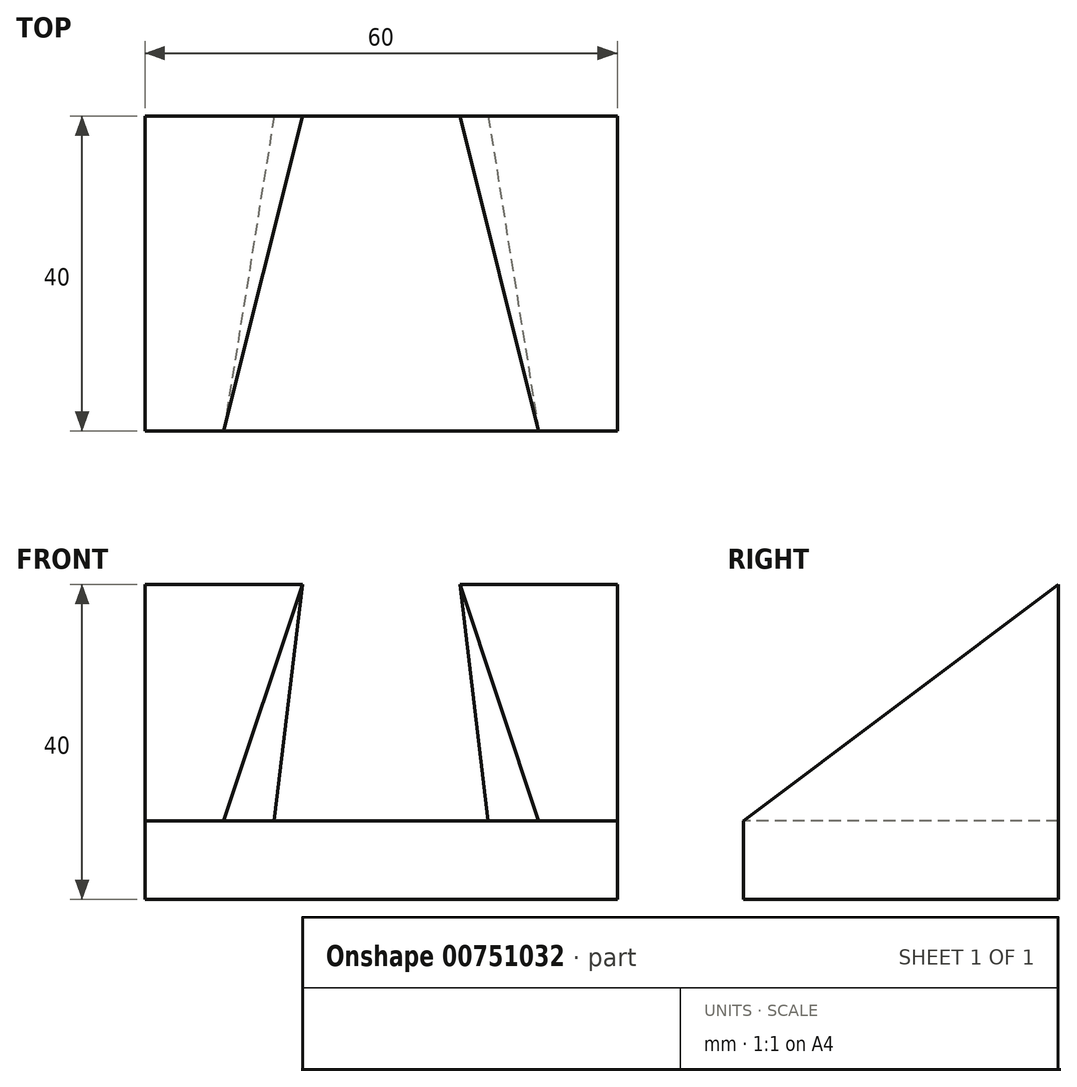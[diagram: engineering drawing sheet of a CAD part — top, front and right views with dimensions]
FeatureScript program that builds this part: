
annotation { "Feature Type Name" : "Feature", "Feature Type Description" : "" }
export const myFeature = defineFeature(function(context is Context, id is Id, definition is map)
    precondition{}
    {
        {
            var Q0;
            Q0=qCreatedBy(makeId("Front.planeOp"),FACE);
            var sketch = newSketch(context, id + "F0", { "sketchPlane" : qUnion([Q0])});
            skLineSegment(sketch, "E0", {"start": v(0, 0) * mm, "end": v(60, 0) * mm});
            skLineSegment(sketch, "E1", {"start": v(60, 0) * mm, "end": v(60, 40) * mm});
            skLineSegment(sketch, "E2", {"start": v(60, 40) * mm, "end": v(40, 40) * mm});
            skLineSegment(sketch, "E3", {"start": v(40, 40) * mm, "end": v(40, 10) * mm});
            skLineSegment(sketch, "E4", {"start": v(40, 10) * mm, "end": v(20, 10) * mm});
            skLineSegment(sketch, "E5", {"start": v(20, 10) * mm, "end": v(20, 40) * mm});
            skLineSegment(sketch, "E6", {"start": v(20, 40) * mm, "end": v(0, 40) * mm});
            skLineSegment(sketch, "E7", {"start": v(0, 40) * mm, "end": v(0, 0) * mm});
            skSolve(sketch);
        }
        {
            var Q0;
            Q0=makeQuery(id+"F0.imprint","IMPRINT",FACE,{"disambiguationData":[TD([[makeQuery(id+"F0.imprint","IMPRINT",EDGE,{"derivedFrom":sQuery(id+"F0.wireOp",EDGE,"E0")}),1.0]])]});
            extrude(context, id + "F1", {"entities" : qUnion([Q0]), "depth" : 40 * mm, "offsetDistance" : 25 * mm});
        }
        {
            var Q0;
            Q0=makeQuery(id+"F1.opExtrude","SWEPT_FACE",FACE,{"disambiguationData":[OSD([sQuery(id+"F0.wireOp",EDGE,"E1")])]});
            var sketch = newSketch(context, id + "F2", { "sketchPlane" : qUnion([Q0])});
            skLineSegment(sketch, "E8", {"start": v(0, 40) * mm, "end": v(0, 10) * mm});
            skLineSegment(sketch, "E9", {"start": v(0, 10) * mm, "end": v(-40, 10) * mm});
            skLineSegment(sketch, "E10", {"start": v(-40, 10) * mm, "end": v(0, 40) * mm});
            skSolve(sketch);
        }
        {
            var Q0;
            {var subQ0=sQuery(id+"F2.wireOp",EDGE,"E10");Q0=makeQuery(id+"F2.imprint","IMPRINT",FACE,{"disambiguationData":[TD([[makeQuery(id+"F2.imprint","IMPRINT",EDGE,{"derivedFrom":subQ0}),1.0]])]});}
            extrude(context, id + "F3", {"entities" : qUnion([Q0]), "operationType" : NewBodyOperationType.REMOVE, "oppositeDirection" : true, "depth" : 60 * mm, "offsetDistance" : 25 * mm});
        }
        {
            var Q0;
            {var subQ0=sQuery(id+"F0.wireOp",EDGE,"E5");Q0=makeQuery(id+"F3.boolean.opBoolean","COPY",FACE,{"disambiguationData":[TD([makeQuery(id+"F1.opExtrude","SWEPT_FACE",FACE,{"disambiguationData":[OSD([subQ0])]})])],"derivedFrom":makeQuery(id+"F3.opExtrude","SWEPT_FACE",FACE,{"disambiguationData":[OSD([sQuery(id+"F2.wireOp",EDGE,"E10")])]})});}
            var sketch = newSketch(context, id + "F4", { "sketchPlane" : qUnion([Q0])});
            skLineSegment(sketch, "E11", {"start": v(20, 24) * mm, "end": v(10, -26) * mm});
            skLineSegment(sketch, "E12", {"start": v(10, -26) * mm, "end": v(20, -26) * mm});
            skLineSegment(sketch, "E13", {"start": v(20, -26) * mm, "end": v(20, 24) * mm});
            skSolve(sketch);
        }
        {
            var Q0;
            Q0=makeQuery(id+"F4.imprint","IMPRINT",FACE,{"disambiguationData":[TD([[makeQuery(id+"F4.imprint","IMPRINT",EDGE,{"derivedFrom":sQuery(id+"F4.wireOp",EDGE,"E11")}),1.0]])]});
            extrude(context, id + "F5", {"entities" : qUnion([Q0]), "operationType" : NewBodyOperationType.REMOVE, "oppositeDirection" : true, "depth" : 40 * mm, "offsetDistance" : 25 * mm});
        }
        {
            var Q0;
            {var subQ1=sQuery(id+"F0.wireOp",EDGE,"E1");Q0=makeQuery(id+"F3.boolean.opBoolean","COPY",FACE,{"disambiguationData":[TD([makeQuery(id+"F1.opExtrude","SWEPT_FACE",FACE,{"disambiguationData":[OSD([subQ1])]})])],"derivedFrom":makeQuery(id+"F3.opExtrude","SWEPT_FACE",FACE,{"disambiguationData":[OSD([sQuery(id+"F2.wireOp",EDGE,"E10")])]})});}
            var sketch = newSketch(context, id + "F6", { "sketchPlane" : qUnion([Q0])});
            skLineSegment(sketch, "E14", {"start": v(40, 24) * mm, "end": v(50, -26) * mm});
            skLineSegment(sketch, "E15", {"start": v(50, -26) * mm, "end": v(40, -26) * mm});
            skLineSegment(sketch, "E16", {"start": v(40, -26) * mm, "end": v(40, 24) * mm});
            skSolve(sketch);
        }
        {
            var Q0;
            Q0=makeQuery(id+"F6.imprint","IMPRINT",FACE,{"disambiguationData":[TD([[makeQuery(id+"F6.imprint","IMPRINT",EDGE,{"derivedFrom":sQuery(id+"F6.wireOp",EDGE,"E14")}),-1.0]])]});
            extrude(context, id + "F7", {"entities" : qUnion([Q0]), "operationType" : NewBodyOperationType.REMOVE, "oppositeDirection" : true, "depth" : 40 * mm, "offsetDistance" : 25 * mm});
        }
        {
            var Q0;
            Q0=makeQuery(id+"F1.opExtrude","CAP_FACE",FACE,{"disambiguationData":[OSD([sQuery(id+"F0.wireOp",EDGE,"E0"),sQuery(id+"F0.wireOp",EDGE,"E1"),sQuery(id+"F0.wireOp",EDGE,"E2"),sQuery(id+"F0.wireOp",EDGE,"E3"),sQuery(id+"F0.wireOp",EDGE,"E4"),sQuery(id+"F0.wireOp",EDGE,"E5"),sQuery(id+"F0.wireOp",EDGE,"E6"),sQuery(id+"F0.wireOp",EDGE,"E7")])],"isStart":false});
            var sketch = newSketch(context, id + "F8", { "sketchPlane" : qUnion([Q0])});
            skLineSegment(sketch, "E17", {"start": v(10, 10) * mm, "end": v(20, 10) * mm});
            skLineSegment(sketch, "E18", {"start": v(20, 10) * mm, "end": v(20, 0) * mm});
            skLineSegment(sketch, "E19", {"start": v(20, 0) * mm, "end": v(10, 0) * mm});
            skLineSegment(sketch, "E20", {"start": v(10, 0) * mm, "end": v(10, 10) * mm});
            skSolve(sketch);
        }
        {
            var Q0;
            Q0=makeQuery(id+"F8.imprint","IMPRINT",FACE,{"disambiguationData":[TD([[makeQuery(id+"F8.imprint","IMPRINT",EDGE,{"derivedFrom":sQuery(id+"F8.wireOp",EDGE,"E17")}),-1.0]])]});
            extrude(context, id + "F9", {"entities" : qUnion([Q0]), "operationType" : NewBodyOperationType.ADD, "oppositeDirection" : true, "depth" : 40 * mm, "offsetDistance" : 25 * mm});
        }
        {
            var Q0;
            Q0=makeQuery(id+"F1.opExtrude","CAP_FACE",FACE,{"disambiguationData":[OSD([sQuery(id+"F0.wireOp",EDGE,"E0"),sQuery(id+"F0.wireOp",EDGE,"E1"),sQuery(id+"F0.wireOp",EDGE,"E2"),sQuery(id+"F0.wireOp",EDGE,"E3"),sQuery(id+"F0.wireOp",EDGE,"E4"),sQuery(id+"F0.wireOp",EDGE,"E5"),sQuery(id+"F0.wireOp",EDGE,"E6"),sQuery(id+"F0.wireOp",EDGE,"E7")])],"isStart":false});
            var sketch = newSketch(context, id + "F10", { "sketchPlane" : qUnion([Q0])});
            skLineSegment(sketch, "E21", {"start": v(50, 10) * mm, "end": v(40, 10) * mm});
            skLineSegment(sketch, "E22", {"start": v(40, 10) * mm, "end": v(40, 0) * mm});
            skLineSegment(sketch, "E23", {"start": v(40, 0) * mm, "end": v(50, 0) * mm});
            skLineSegment(sketch, "E24", {"start": v(50, 0) * mm, "end": v(50, 10) * mm});
            skSolve(sketch);
        }
        {
            var Q0;
            Q0=makeQuery(id+"F10.imprint","IMPRINT",FACE,{"disambiguationData":[TD([[makeQuery(id+"F10.imprint","IMPRINT",EDGE,{"derivedFrom":sQuery(id+"F10.wireOp",EDGE,"E21")}),-1.0]])]});
            extrude(context, id + "F11", {"entities" : qUnion([Q0]), "operationType" : NewBodyOperationType.ADD, "oppositeDirection" : true, "depth" : 40 * mm, "offsetDistance" : 25 * mm});
        }
    });
